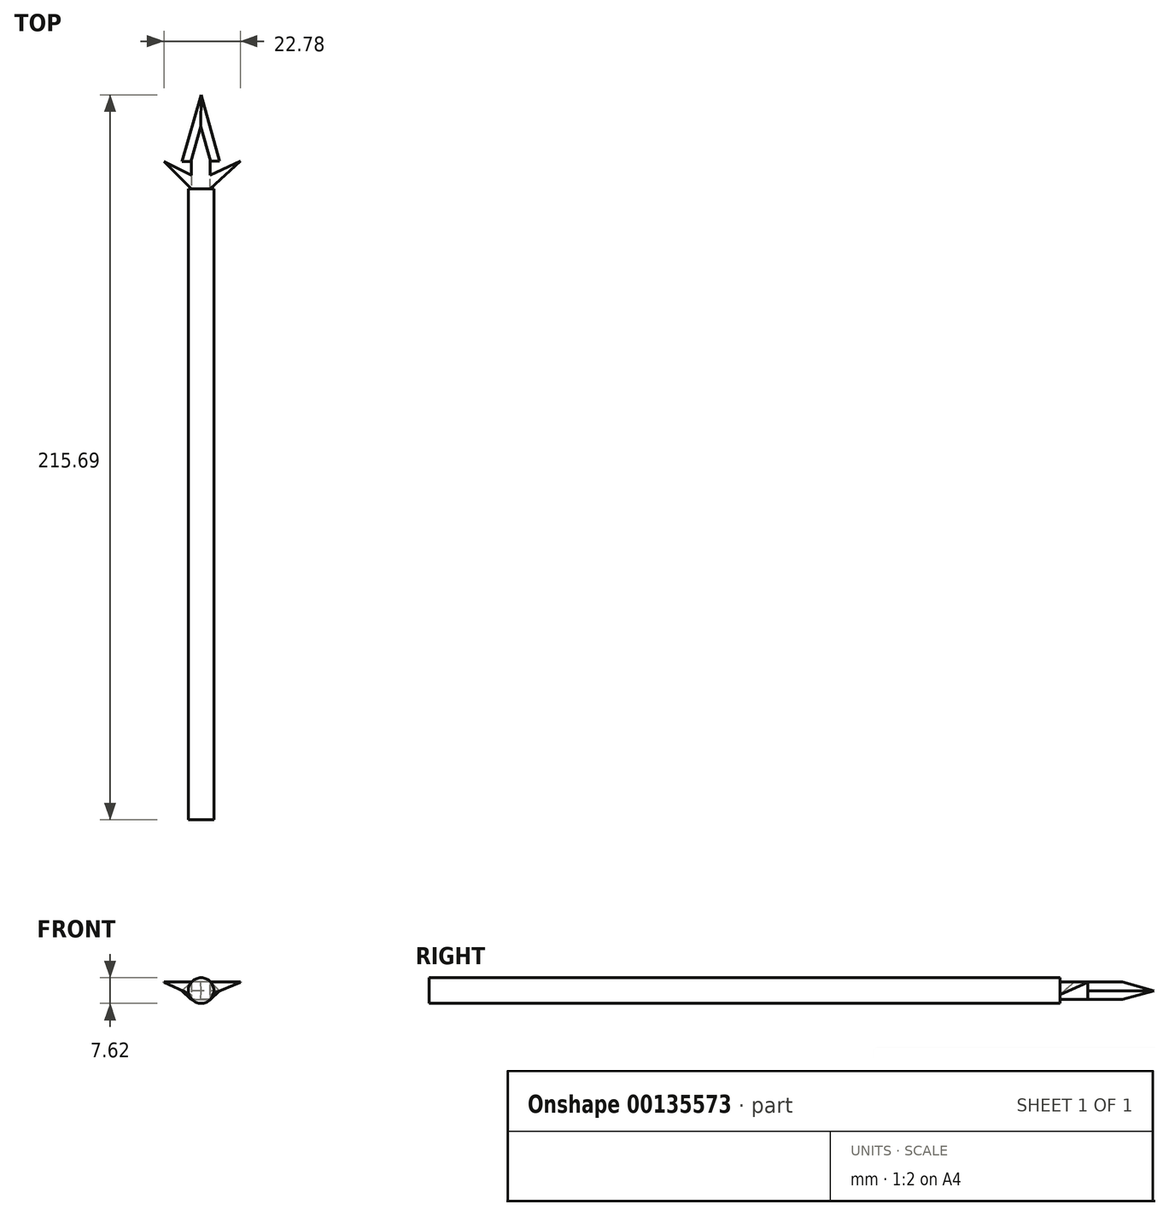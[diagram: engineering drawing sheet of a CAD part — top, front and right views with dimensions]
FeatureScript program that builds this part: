
annotation { "Feature Type Name" : "Feature", "Feature Type Description" : "" }
export const myFeature = defineFeature(function(context is Context, id is Id, definition is map)
    precondition{}
    {
        {
            var Q0;
            Q0=qCreatedBy(makeId("Front.planeOp"),FACE);
            var sketch = newSketch(context, id + "F0", { "sketchPlane" : qUnion([Q0])});
            skCircle(sketch, "E0", {"center": v(0, 0) * mm, "radius": 3.81 * mm});
            skSolve(sketch);
        }
        {
            var Q0;
            Q0 = qSketchRegion(id + "F0", true);
            extrude(context, id + "F1", {"entities" : qUnion([Q0]), "oppositeDirection" : true, "depth" : 187.71 * mm});
        }
        {
            var Q0;
            Q0=qCreatedBy(makeId("Top.planeOp"),FACE);
            var sketch = newSketch(context, id + "F2", { "sketchPlane" : qUnion([Q0])});
            skLineSegment(sketch, "E1", {"start": v(-2.89, 187.74) * mm, "end": v(-2.89, 195.88) * mm});
            skLineSegment(sketch, "E2", {"start": v(2.73, 187.72) * mm, "end": v(2.73, 195.93) * mm});
            skLineSegment(sketch, "E3", {"start": v(2.73, 187.72) * mm, "end": v(-2.89, 187.74) * mm});
            skLineSegment(sketch, "E4", {"start": v(-2.89, 195.88) * mm, "end": v(-8.3, 195.88) * mm});
            skLineSegment(sketch, "E5", {"start": v(-8.3, 195.88) * mm, "end": v(0, 224.9) * mm});
            skLineSegment(sketch, "E6", {"start": v(2.73, 195.93) * mm, "end": v(8.11, 195.93) * mm});
            skLineSegment(sketch, "E7", {"start": v(8.11, 195.93) * mm, "end": v(0, 224.9) * mm});
            skLineSegment(sketch, "E8", {"start": v(-2.89, 191.81) * mm, "end": v(-11.07, 195.88) * mm});
            skLineSegment(sketch, "E9", {"start": v(-11.07, 195.88) * mm, "end": v(-2.89, 187.74) * mm});
            skLineSegment(sketch, "E10", {"start": v(2.73, 187.72) * mm, "end": v(11.7, 195.93) * mm});
            skLineSegment(sketch, "E11", {"start": v(11.7, 195.93) * mm, "end": v(2.73, 191.83) * mm});
            skSolve(sketch);
        }
        {
            var Q0;
            {var subQ3=sQuery(id+"F2.wireOp",EDGE,"E3");Q0=makeQuery(id+"F2.imprint","IMPRINT",FACE,{"disambiguationData":[TD([[makeQuery(id+"F2.imprint","IMPRINT",EDGE,{"derivedFrom":subQ3}),-1.0]])]});}
            var Q1;
            {var subQ2=sQuery(id+"F2.wireOp",EDGE,"E8");Q1=makeQuery(id+"F2.imprint","IMPRINT",FACE,{"disambiguationData":[TD([[makeQuery(id+"F2.imprint","IMPRINT",EDGE,{"derivedFrom":subQ2}),1.0]])]});}
            var Q2;
            {var subQ0=sQuery(id+"F2.wireOp",EDGE,"E10");Q2=makeQuery(id+"F2.imprint","IMPRINT",FACE,{"disambiguationData":[TD([[makeQuery(id+"F2.imprint","IMPRINT",EDGE,{"derivedFrom":subQ0}),1.0]])]});}
            extrude(context, id + "F3", {"entities" : qUnion([Q0, Q1, Q2]), "operationType" : NewBodyOperationType.ADD, "depth" : 2.54 * mm, "hasSecondDirection" : true, "secondDirectionOppositeDirection" : true, "secondDirectionDepth" : 2.6 * mm});
        }
        {
            var Q0;
            Q0=makeQuery(id+"F3.opExtrude","CAP_EDGE",EDGE,{"disambiguationData":[OSD([sQuery(id+"F2.wireOp",EDGE,"E7")])],"isStart":true});
            var Q1;
            Q1=makeQuery(id+"F3.opExtrude","CAP_EDGE",EDGE,{"disambiguationData":[OSD([sQuery(id+"F2.wireOp",EDGE,"E5")])],"isStart":true});
            chamfer(context, id + "F4", {"entities" : qUnion([Q0, Q1]), "width" : 5.08 * mm, "tangentPropagation" : true});
        }
        {
            var Q0;
            Q0=makeQuery(id+"F3.opExtrude","CAP_EDGE",EDGE,{"disambiguationData":[OSD([sQuery(id+"F2.wireOp",EDGE,"E7")])],"isStart":false});
            var Q1;
            Q1=makeQuery(id+"F3.opExtrude","CAP_EDGE",EDGE,{"disambiguationData":[OSD([sQuery(id+"F2.wireOp",EDGE,"E5")])],"isStart":false});
            chamfer(context, id + "F5", {"entities" : qUnion([Q0, Q1]), "width" : 5.08 * mm, "tangentPropagation" : true});
        }
        {
            var Q0;
            Q0=makeQuery(id+"F3.opExtrude","CAP_EDGE",EDGE,{"disambiguationData":[OSD([sQuery(id+"F2.wireOp",EDGE,"E8")])],"isStart":true});
            var Q1;
            Q1=makeQuery(id+"F3.opExtrude","CAP_EDGE",EDGE,{"disambiguationData":[OSD([sQuery(id+"F2.wireOp",EDGE,"E11")])],"isStart":true});
            chamfer(context, id + "F6", {"entities" : qUnion([Q0, Q1]), "width" : 5.08 * mm, "tangentPropagation" : true});
        }
    });
